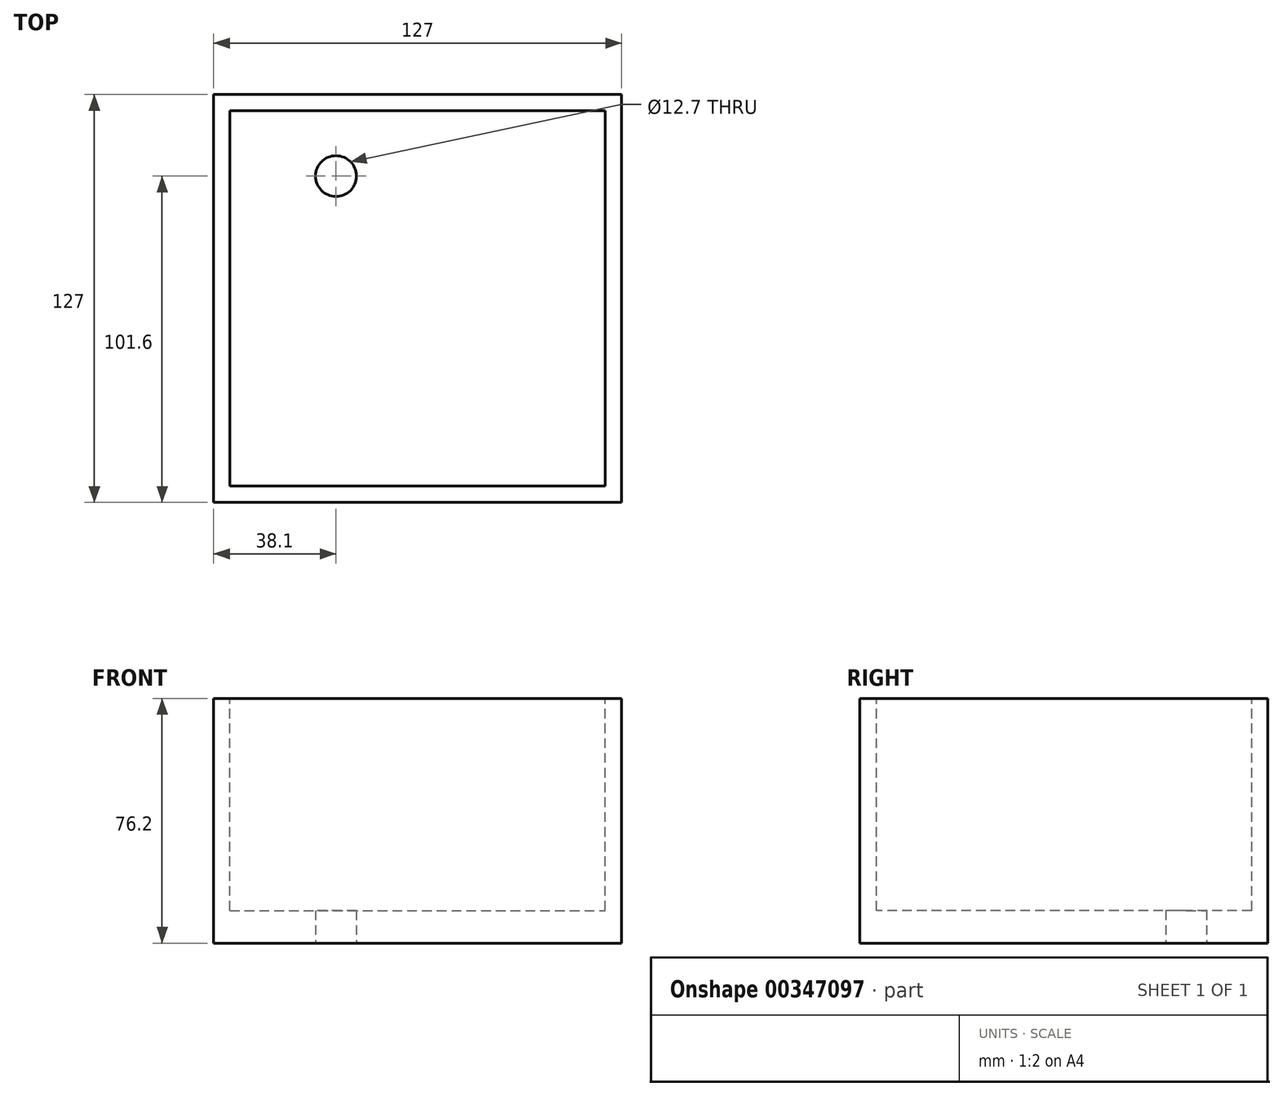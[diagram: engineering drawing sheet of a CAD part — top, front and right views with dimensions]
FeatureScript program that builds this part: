
annotation { "Feature Type Name" : "Feature", "Feature Type Description" : "" }
export const myFeature = defineFeature(function(context is Context, id is Id, definition is map)
    precondition{}
    {
        {
            var Q0;
            Q0=qCreatedBy(makeId("Top.planeOp"),FACE);
            var sketch = newSketch(context, id + "F0", { "sketchPlane" : qUnion([Q0])});
            skLineSegment(sketch, "E0.bottom", {"start": v(63.5, -63.5) * mm, "end": v(-63.5, -63.5) * mm});
            skLineSegment(sketch, "E0.top", {"start": v(63.5, 63.5) * mm, "end": v(-63.5, 63.5) * mm});
            skLineSegment(sketch, "E0.left", {"start": v(63.5, -63.5) * mm, "end": v(63.5, 63.5) * mm});
            skLineSegment(sketch, "E0.right", {"start": v(-63.5, -63.5) * mm, "end": v(-63.5, 63.5) * mm});
            skPoint(sketch, "E0.middle", {"position": v(0, 0) * mm});
            skSolve(sketch);
        }
        {
            var Q0;
            Q0 = qSketchRegion(id + "F0", true);
            extrude(context, id + "F1", {"entities" : qUnion([Q0]), "depth" : 76.2 * mm});
        }
        {
            var Q0;
            Q0=makeQuery(id+"F1.opExtrude","CAP_FACE",FACE,{"disambiguationData":[OSD([sQuery(id+"F0.wireOp",EDGE,"E0.bottom"),sQuery(id+"F0.wireOp",EDGE,"E0.top"),sQuery(id+"F0.wireOp",EDGE,"E0.left"),sQuery(id+"F0.wireOp",EDGE,"E0.right")])],"isStart":false});
            var sketch = newSketch(context, id + "F2", { "sketchPlane" : qUnion([Q0])});
            skLineSegment(sketch, "E1.bottom", {"start": v(-58.42, 58.42) * mm, "end": v(58.42, 58.42) * mm});
            skLineSegment(sketch, "E1.top", {"start": v(-58.42, -58.42) * mm, "end": v(58.42, -58.42) * mm});
            skLineSegment(sketch, "E1.left", {"start": v(-58.42, 58.42) * mm, "end": v(-58.42, -58.42) * mm});
            skLineSegment(sketch, "E1.right", {"start": v(58.42, 58.42) * mm, "end": v(58.42, -58.42) * mm});
            skPoint(sketch, "E1.middle", {"position": v(0, 0) * mm});
            skSolve(sketch);
        }
        {
            var Q0;
            Q0 = qSketchRegion(id + "F2", true);
            extrude(context, id + "F3", {"entities" : qUnion([Q0]), "operationType" : NewBodyOperationType.REMOVE, "oppositeDirection" : true, "depth" : 66.04 * mm});
        }
        {
            var Q0;
            Q0=makeQuery(id+"F1.opExtrude","CAP_FACE",FACE,{"disambiguationData":[OSD([sQuery(id+"F0.wireOp",EDGE,"E0.bottom"),sQuery(id+"F0.wireOp",EDGE,"E0.top"),sQuery(id+"F0.wireOp",EDGE,"E0.left"),sQuery(id+"F0.wireOp",EDGE,"E0.right")])],"isStart":true});
            var sketch = newSketch(context, id + "F4", { "sketchPlane" : qUnion([Q0])});
            skPoint(sketch, "E2", {"position": v(-25.4, -38.1) * mm});
            skCircle(sketch, "E3", {"center": v(-25.4, -38.1) * mm, "radius": 6.35 * mm});
            skSolve(sketch);
        }
        {
            var Q0;
            Q0 = qSketchRegion(id + "F4", true);
            extrude(context, id + "F5", {"entities" : qUnion([Q0]), "operationType" : NewBodyOperationType.REMOVE, "endBound" : BoundingType.THROUGH_ALL, "oppositeDirection" : true, "depth" : 25.4 * mm});
        }
    });
